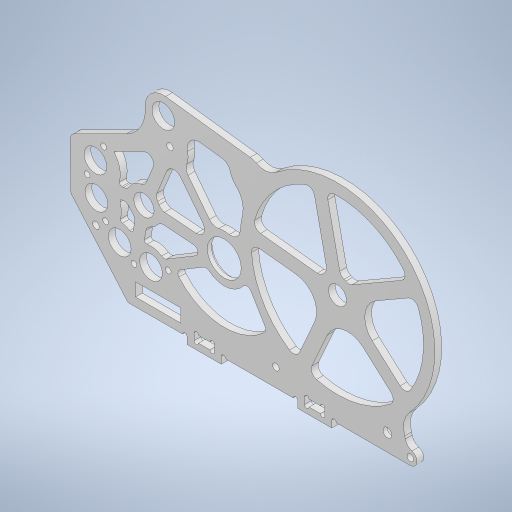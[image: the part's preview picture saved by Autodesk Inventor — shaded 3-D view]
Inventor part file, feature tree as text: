
AUTODESK INVENTOR PART (.ipt)
format: ipt  version: 2023.1 (Build 271208000, 208)  size: 988,672 bytes
history: native  units: mm
features: sketch x3, extrude x3, other x1, fillet x1, projected_geometry x1
ambient origin geometry x8: Origin, YZ Plane, XZ Plane, XY Plane, X Axis, Y Axis, Z Axis, Center Point
bodies: Body1 (feature_tree)
feature tree (9):
  other  "ソリッド1"
  sketch  "スケッチ1"
  extrude  "押し出し1"  Depth=6.0mm
  extrude  "押し出し2"  Depth=8.0mm
  fillet  "フィレット1"  Radius=4.0mm
  sketch  "スケッチ2"
  extrude  "押し出し3"  Depth=3.0mm TaperAngle=0.0deg
  projected_geometry  "投影ループ1"
  sketch  "スケッチ3"
